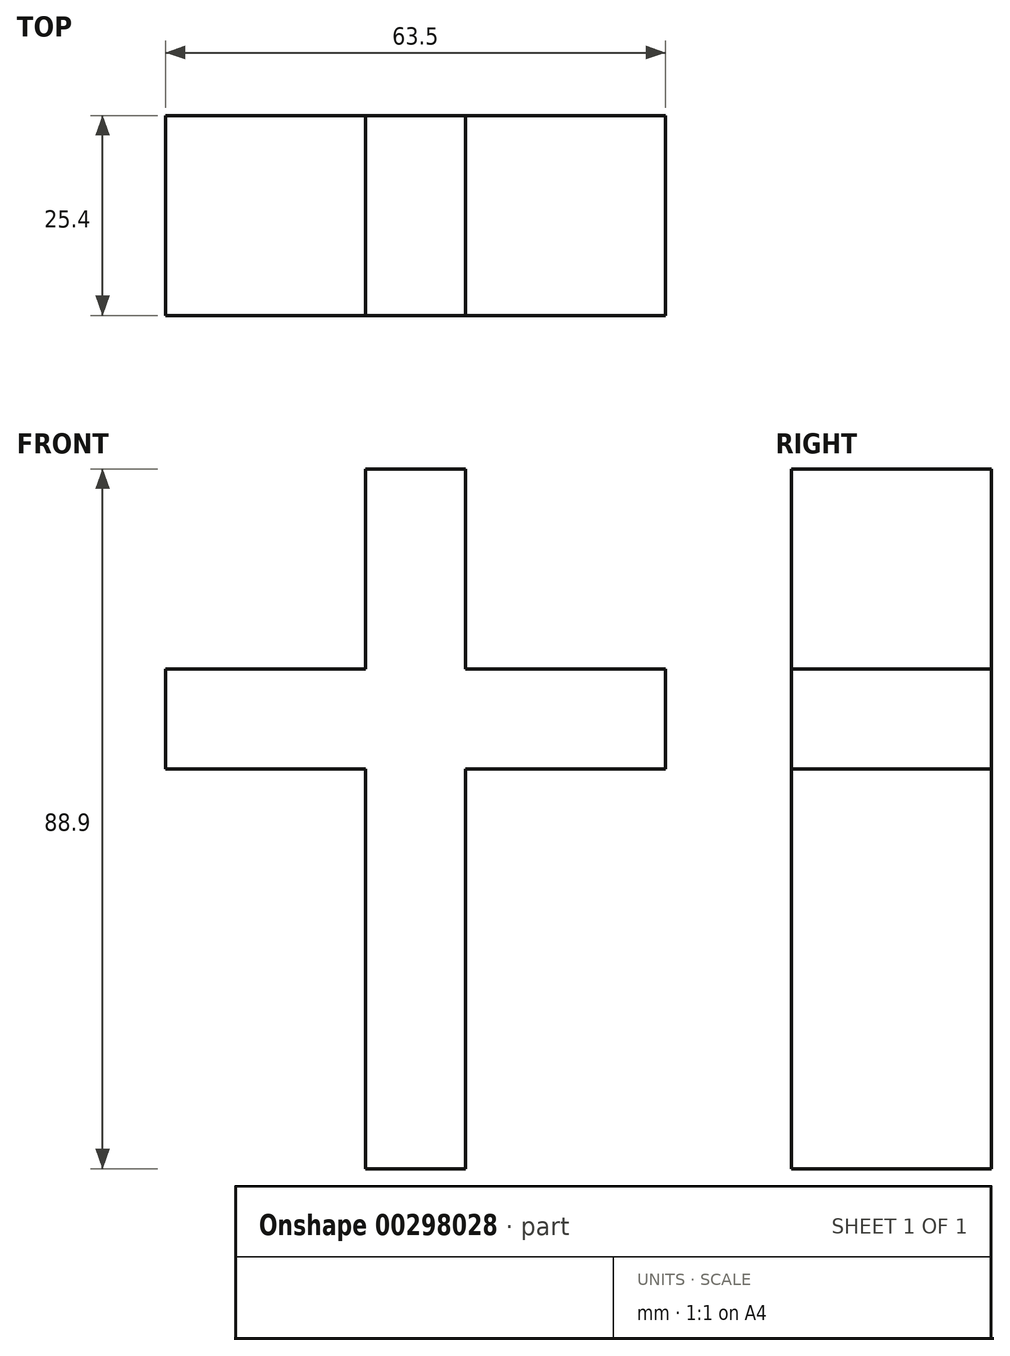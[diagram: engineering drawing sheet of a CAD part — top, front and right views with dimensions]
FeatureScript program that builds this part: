
annotation { "Feature Type Name" : "Feature", "Feature Type Description" : "" }
export const myFeature = defineFeature(function(context is Context, id is Id, definition is map)
    precondition{}
    {
        {
            var Q0;
            Q0=qCreatedBy(makeId("Front.planeOp"),FACE);
            var sketch = newSketch(context, id + "F0", { "sketchPlane" : qUnion([Q0])});
            skLineSegment(sketch, "E0", {"start": v(0, 0) * mm, "end": v(-12.7, 0) * mm});
            skLineSegment(sketch, "E1", {"start": v(-12.7, 0) * mm, "end": v(-12.7, 50.8) * mm});
            skLineSegment(sketch, "E2", {"start": v(-12.7, 50.8) * mm, "end": v(-38.1, 50.8) * mm});
            skLineSegment(sketch, "E3", {"start": v(-38.1, 50.8) * mm, "end": v(-38.1, 63.5) * mm});
            skLineSegment(sketch, "E4", {"start": v(-38.1, 63.5) * mm, "end": v(-12.7, 63.5) * mm});
            skLineSegment(sketch, "E5", {"start": v(-12.7, 63.5) * mm, "end": v(-12.7, 88.9) * mm});
            skLineSegment(sketch, "E6", {"start": v(-12.7, 88.9) * mm, "end": v(0, 88.9) * mm});
            skLineSegment(sketch, "E7", {"start": v(0, 88.9) * mm, "end": v(0, 63.5) * mm});
            skLineSegment(sketch, "E8", {"start": v(0, 63.5) * mm, "end": v(25.4, 63.5) * mm});
            skLineSegment(sketch, "E9", {"start": v(25.4, 63.5) * mm, "end": v(25.4, 50.8) * mm});
            skLineSegment(sketch, "E10", {"start": v(25.4, 50.8) * mm, "end": v(0, 50.8) * mm});
            skLineSegment(sketch, "E11", {"start": v(0, 50.8) * mm, "end": v(0, 0) * mm});
            skSolve(sketch);
        }
        {
            var Q0;
            Q0 = qSketchRegion(id + "F0", true);
            extrude(context, id + "F1", {"entities" : qUnion([Q0]), "depth" : 25.4 * mm});
        }
    });
